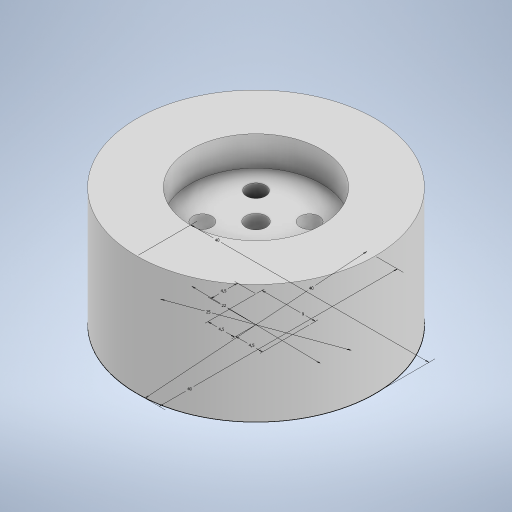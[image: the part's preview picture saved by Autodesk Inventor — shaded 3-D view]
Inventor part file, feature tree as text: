
AUTODESK INVENTOR PART (.ipt)
format: ipt  version: 2023 (Build 270158000, 158)  size: 240,640 bytes
history: native  units: in
note: dims shown in document units (in); Inventor stores cm internally (conversion verified against a paired STEP export)
features: extrude x2, hole x2, other x1, sketch x1
ambient origin geometry x8: Origin, YZ Plane, XZ Plane, XY Plane, X Axis, Y Axis, Z Axis, Center Point
bodies: Body1 (feature_tree)
feature tree (6):
  other  "Bryła1"
  sketch  "Szkic1"
  extrude  "Wyciągnięcie proste1"  Depth=1.5748in
  extrude  "Wyciągnięcie proste2"  Depth=0.9843in
  hole  "Otwór2"  [1 undecoded]
  hole  "Hole4"  [1 undecoded]
note: 2 required parameter values undecoded (feature->parameter linkage not recoverable at this tier; creation-order binding heuristic only, values carry confidence <= 0.55)
